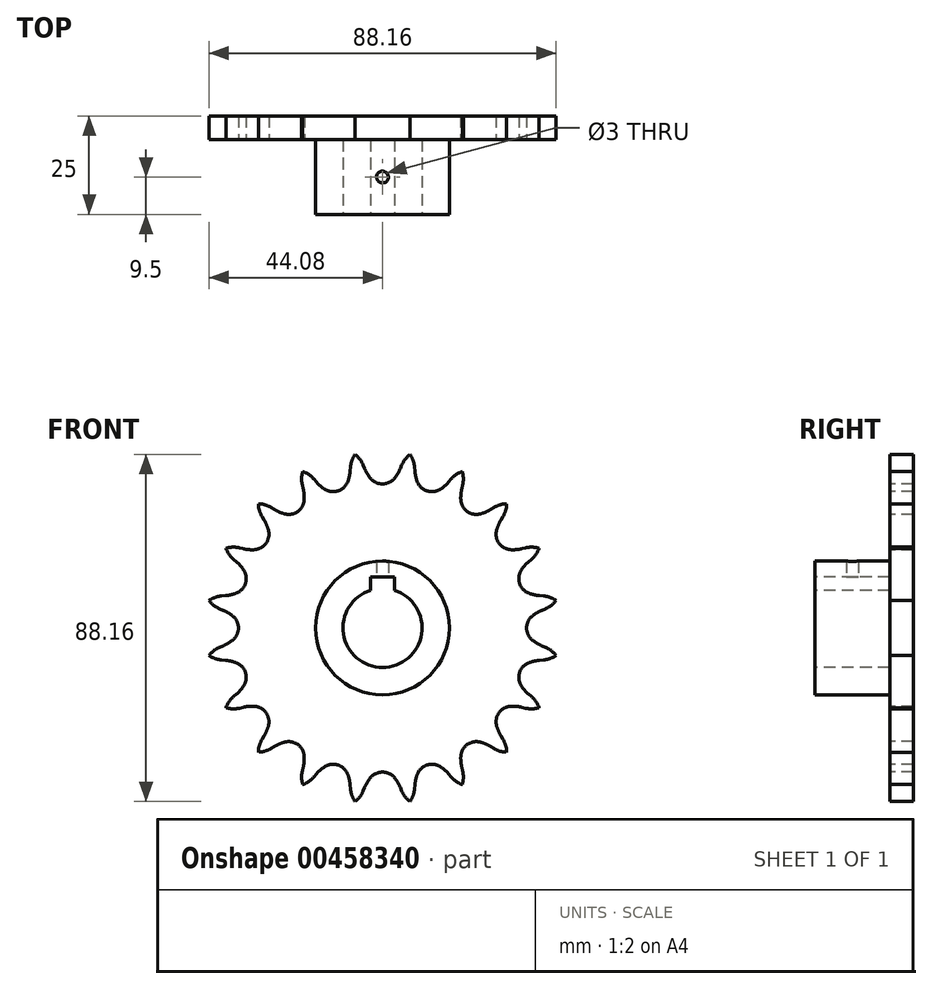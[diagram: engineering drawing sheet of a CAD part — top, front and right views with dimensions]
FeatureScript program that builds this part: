
annotation { "Feature Type Name" : "Feature", "Feature Type Description" : "" }
export const myFeature = defineFeature(function(context is Context, id is Id, definition is map)
    precondition{}
    {
        {
            var Q0;
            Q0=qCreatedBy(makeId("Front.planeOp"),FACE);
            var sketch = newSketch(context, id + "F0", { "sketchPlane" : qUnion([Q0])});
            skCircle(sketch, "E0", {"center": v(0, 0) * mm, "radius": 40.6 * mm, "construction": true});
            skLineSegment(sketch, "E1", {"start": v(0, 0) * mm, "end": v(0, 40.6) * mm, "construction": true});
            skLineSegment(sketch, "E2", {"start": v(0, 40.6) * mm, "end": v(73.85, 40.6) * mm, "construction": true});
            skArc(sketch, "E3", {"start": v(-3.14, 38.14) * mm, "mid": v(-1.75, 37.01) * mm, "end": v(0, 36.61) * mm});
            skLineSegment(sketch, "E4", {"start": v(0, 40.6) * mm, "end": v(5, 44.5) * mm, "construction": true});
            skLineSegment(sketch, "E5", {"start": v(5, 44.5) * mm, "end": v(-4.52, 40.5) * mm, "construction": true});
            skLineSegment(sketch, "E6", {"start": v(-4.52, 40.5) * mm, "end": v(-4.9, 41.4) * mm});
            skArc(sketch, "E7", {"start": v(-4.52, 40.5) * mm, "mid": v(-3.9, 39.27) * mm, "end": v(-3.14, 38.14) * mm});
            skArc(sketch, "E8", {"start": v(-17.18, 36.78) * mm, "mid": v(-9.17, 32.53) * mm, "end": v(-4.55, 40.34) * mm, "construction": true});
            skLineSegment(sketch, "E9", {"start": v(0, -0.5) * mm, "end": v(-9.94, 62.24) * mm, "construction": true});
            skArc(sketch, "E10.trimOffspring", {"start": v(-4.9, 41.4) * mm, "mid": v(-5.8, 42.92) * mm, "end": v(-7.07, 44.15) * mm});
            skArc(sketch, "E11.trimOffspring", {"start": v(0, 35.46) * mm, "mid": v(8.42, 34.76) * mm, "end": v(14.54, 40.6) * mm, "construction": true});
            skArc(sketch, "E12.trimOffspring", {"start": v(3.98, 40.4) * mm, "mid": v(3.98, 40.5) * mm, "end": v(3.98, 40.6) * mm, "construction": true});
            skArc(sketch, "E13.MirrorCS", {"start": v(4.9, 41.4) * mm, "mid": v(5.8, 42.92) * mm, "end": v(7.07, 44.15) * mm});
            skLineSegment(sketch, "E14.MirrorCS", {"start": v(4.52, 40.5) * mm, "end": v(4.9, 41.4) * mm});
            skArc(sketch, "E15.MirrorCS", {"start": v(4.52, 40.5) * mm, "mid": v(3.9, 39.27) * mm, "end": v(3.14, 38.14) * mm});
            skArc(sketch, "E16.MirrorCS", {"start": v(3.14, 38.14) * mm, "mid": v(1.75, 37.01) * mm, "end": v(0, 36.61) * mm});
            skArc(sketch, "E17.1.0", {"start": v(-8.14, 40.88) * mm, "mid": v(-7.75, 42.6) * mm, "end": v(-6.92, 44.17) * mm});
            skLineSegment(sketch, "E17.1.1", {"start": v(-8.22, 39.9) * mm, "end": v(-8.14, 40.88) * mm});
            skArc(sketch, "E17.1.2", {"start": v(-8.22, 39.9) * mm, "mid": v(-8.42, 38.56) * mm, "end": v(-8.8, 37.24) * mm});
            skArc(sketch, "E17.1.3", {"start": v(-8.8, 37.24) * mm, "mid": v(-9.78, 35.74) * mm, "end": v(-11.31, 34.82) * mm});
            skArc(sketch, "E17.1.4", {"start": v(-14.77, 35.3) * mm, "mid": v(-13.1, 34.66) * mm, "end": v(-11.31, 34.82) * mm});
            skArc(sketch, "E17.1.5", {"start": v(-16.81, 37.12) * mm, "mid": v(-15.85, 36.14) * mm, "end": v(-14.77, 35.3) * mm});
            skLineSegment(sketch, "E17.1.6", {"start": v(-16.81, 37.12) * mm, "end": v(-17.45, 37.85) * mm});
            skArc(sketch, "E17.1.7", {"start": v(-17.45, 37.85) * mm, "mid": v(-18.77, 39.03) * mm, "end": v(-20.37, 39.8) * mm});
            skArc(sketch, "E17.2.0", {"start": v(-20.37, 36.36) * mm, "mid": v(-20.54, 38.13) * mm, "end": v(-20.23, 39.87) * mm});
            skLineSegment(sketch, "E17.2.1", {"start": v(-20.15, 35.42) * mm, "end": v(-20.37, 36.36) * mm});
            skArc(sketch, "E17.2.2", {"start": v(-20.15, 35.42) * mm, "mid": v(-19.92, 34.07) * mm, "end": v(-19.88, 32.7) * mm});
            skArc(sketch, "E17.2.3", {"start": v(-19.88, 32.7) * mm, "mid": v(-20.34, 30.97) * mm, "end": v(-21.52, 29.62) * mm});
            skArc(sketch, "E17.2.4", {"start": v(-24.96, 29.01) * mm, "mid": v(-23.17, 28.92) * mm, "end": v(-21.52, 29.62) * mm});
            skArc(sketch, "E17.2.5", {"start": v(-27.46, 30.1) * mm, "mid": v(-26.24, 29.48) * mm, "end": v(-24.96, 29.01) * mm});
            skLineSegment(sketch, "E17.2.6", {"start": v(-27.46, 30.1) * mm, "end": v(-28.29, 30.6) * mm});
            skArc(sketch, "E17.2.7", {"start": v(-28.29, 30.6) * mm, "mid": v(-29.92, 31.31) * mm, "end": v(-31.67, 31.56) * mm});
            skArc(sketch, "E17.3.0", {"start": v(-30.6, 28.29) * mm, "mid": v(-31.31, 29.92) * mm, "end": v(-31.56, 31.67) * mm});
            skLineSegment(sketch, "E17.3.1", {"start": v(-30.1, 27.46) * mm, "end": v(-30.6, 28.29) * mm});
            skArc(sketch, "E17.3.2", {"start": v(-30.1, 27.46) * mm, "mid": v(-29.48, 26.24) * mm, "end": v(-29.01, 24.96) * mm});
            skArc(sketch, "E17.3.3", {"start": v(-29.01, 24.96) * mm, "mid": v(-28.92, 23.17) * mm, "end": v(-29.62, 21.52) * mm});
            skArc(sketch, "E17.3.4", {"start": v(-32.7, 19.88) * mm, "mid": v(-30.97, 20.34) * mm, "end": v(-29.62, 21.52) * mm});
            skArc(sketch, "E17.3.5", {"start": v(-35.42, 20.15) * mm, "mid": v(-34.07, 19.92) * mm, "end": v(-32.7, 19.88) * mm});
            skLineSegment(sketch, "E17.3.6", {"start": v(-35.42, 20.15) * mm, "end": v(-36.36, 20.37) * mm});
            skArc(sketch, "E17.3.7", {"start": v(-36.36, 20.37) * mm, "mid": v(-38.13, 20.54) * mm, "end": v(-39.87, 20.23) * mm});
            skArc(sketch, "E17.4.0", {"start": v(-37.85, 17.45) * mm, "mid": v(-39.03, 18.77) * mm, "end": v(-39.8, 20.37) * mm});
            skLineSegment(sketch, "E17.4.1", {"start": v(-37.12, 16.81) * mm, "end": v(-37.85, 17.45) * mm});
            skArc(sketch, "E17.4.2", {"start": v(-37.12, 16.81) * mm, "mid": v(-36.14, 15.85) * mm, "end": v(-35.3, 14.77) * mm});
            skArc(sketch, "E17.4.3", {"start": v(-35.3, 14.77) * mm, "mid": v(-34.66, 13.1) * mm, "end": v(-34.82, 11.31) * mm});
            skArc(sketch, "E17.4.4", {"start": v(-37.24, 8.8) * mm, "mid": v(-35.74, 9.78) * mm, "end": v(-34.82, 11.31) * mm});
            skArc(sketch, "E17.4.5", {"start": v(-39.9, 8.22) * mm, "mid": v(-38.56, 8.42) * mm, "end": v(-37.24, 8.8) * mm});
            skLineSegment(sketch, "E17.4.6", {"start": v(-39.9, 8.22) * mm, "end": v(-40.88, 8.14) * mm});
            skArc(sketch, "E17.4.7", {"start": v(-40.88, 8.14) * mm, "mid": v(-42.6, 7.75) * mm, "end": v(-44.17, 6.92) * mm});
            skArc(sketch, "E17.5.0", {"start": v(-41.4, 4.9) * mm, "mid": v(-42.92, 5.8) * mm, "end": v(-44.15, 7.07) * mm});
            skLineSegment(sketch, "E17.5.1", {"start": v(-40.5, 4.52) * mm, "end": v(-41.4, 4.9) * mm});
            skArc(sketch, "E17.5.2", {"start": v(-40.5, 4.52) * mm, "mid": v(-39.27, 3.9) * mm, "end": v(-38.14, 3.14) * mm});
            skArc(sketch, "E17.5.3", {"start": v(-38.14, 3.14) * mm, "mid": v(-37.01, 1.75) * mm, "end": v(-36.61, 0) * mm});
            skArc(sketch, "E17.5.4", {"start": v(-38.14, -3.14) * mm, "mid": v(-37.01, -1.75) * mm, "end": v(-36.61, 0) * mm});
            skArc(sketch, "E17.5.5", {"start": v(-40.5, -4.52) * mm, "mid": v(-39.27, -3.9) * mm, "end": v(-38.14, -3.14) * mm});
            skLineSegment(sketch, "E17.5.6", {"start": v(-40.5, -4.52) * mm, "end": v(-41.4, -4.9) * mm});
            skArc(sketch, "E17.5.7", {"start": v(-41.4, -4.9) * mm, "mid": v(-42.92, -5.8) * mm, "end": v(-44.15, -7.07) * mm});
            skArc(sketch, "E17.6.0", {"start": v(-40.88, -8.14) * mm, "mid": v(-42.6, -7.75) * mm, "end": v(-44.17, -6.92) * mm});
            skLineSegment(sketch, "E17.6.1", {"start": v(-39.9, -8.22) * mm, "end": v(-40.88, -8.14) * mm});
            skArc(sketch, "E17.6.2", {"start": v(-39.9, -8.22) * mm, "mid": v(-38.56, -8.42) * mm, "end": v(-37.24, -8.8) * mm});
            skArc(sketch, "E17.6.3", {"start": v(-37.24, -8.8) * mm, "mid": v(-35.74, -9.78) * mm, "end": v(-34.82, -11.31) * mm});
            skArc(sketch, "E17.6.4", {"start": v(-35.3, -14.77) * mm, "mid": v(-34.66, -13.1) * mm, "end": v(-34.82, -11.31) * mm});
            skArc(sketch, "E17.6.5", {"start": v(-37.12, -16.81) * mm, "mid": v(-36.14, -15.85) * mm, "end": v(-35.3, -14.77) * mm});
            skLineSegment(sketch, "E17.6.6", {"start": v(-37.12, -16.81) * mm, "end": v(-37.85, -17.45) * mm});
            skArc(sketch, "E17.6.7", {"start": v(-37.85, -17.45) * mm, "mid": v(-39.03, -18.77) * mm, "end": v(-39.8, -20.37) * mm});
            skArc(sketch, "E17.7.0", {"start": v(-36.36, -20.37) * mm, "mid": v(-38.13, -20.54) * mm, "end": v(-39.87, -20.23) * mm});
            skLineSegment(sketch, "E17.7.1", {"start": v(-35.42, -20.15) * mm, "end": v(-36.36, -20.37) * mm});
            skArc(sketch, "E17.7.2", {"start": v(-35.42, -20.15) * mm, "mid": v(-34.07, -19.92) * mm, "end": v(-32.7, -19.88) * mm});
            skArc(sketch, "E17.7.3", {"start": v(-32.7, -19.88) * mm, "mid": v(-30.97, -20.34) * mm, "end": v(-29.62, -21.52) * mm});
            skArc(sketch, "E17.7.4", {"start": v(-29.01, -24.96) * mm, "mid": v(-28.92, -23.17) * mm, "end": v(-29.62, -21.52) * mm});
            skArc(sketch, "E17.7.5", {"start": v(-30.1, -27.46) * mm, "mid": v(-29.48, -26.24) * mm, "end": v(-29.01, -24.96) * mm});
            skLineSegment(sketch, "E17.7.6", {"start": v(-30.1, -27.46) * mm, "end": v(-30.6, -28.29) * mm});
            skArc(sketch, "E17.7.7", {"start": v(-30.6, -28.29) * mm, "mid": v(-31.31, -29.92) * mm, "end": v(-31.56, -31.67) * mm});
            skArc(sketch, "E17.8.0", {"start": v(-28.29, -30.6) * mm, "mid": v(-29.92, -31.31) * mm, "end": v(-31.67, -31.56) * mm});
            skLineSegment(sketch, "E17.8.1", {"start": v(-27.46, -30.1) * mm, "end": v(-28.29, -30.6) * mm});
            skArc(sketch, "E17.8.2", {"start": v(-27.46, -30.1) * mm, "mid": v(-26.24, -29.48) * mm, "end": v(-24.96, -29.01) * mm});
            skArc(sketch, "E17.8.3", {"start": v(-24.96, -29.01) * mm, "mid": v(-23.17, -28.92) * mm, "end": v(-21.52, -29.62) * mm});
            skArc(sketch, "E17.8.4", {"start": v(-19.88, -32.7) * mm, "mid": v(-20.34, -30.97) * mm, "end": v(-21.52, -29.62) * mm});
            skArc(sketch, "E17.8.5", {"start": v(-20.15, -35.42) * mm, "mid": v(-19.92, -34.07) * mm, "end": v(-19.88, -32.7) * mm});
            skLineSegment(sketch, "E17.8.6", {"start": v(-20.15, -35.42) * mm, "end": v(-20.37, -36.36) * mm});
            skArc(sketch, "E17.8.7", {"start": v(-20.37, -36.36) * mm, "mid": v(-20.54, -38.13) * mm, "end": v(-20.23, -39.87) * mm});
            skArc(sketch, "E17.9.0", {"start": v(-17.45, -37.85) * mm, "mid": v(-18.77, -39.03) * mm, "end": v(-20.37, -39.8) * mm});
            skLineSegment(sketch, "E17.9.1", {"start": v(-16.81, -37.12) * mm, "end": v(-17.45, -37.85) * mm});
            skArc(sketch, "E17.9.2", {"start": v(-16.81, -37.12) * mm, "mid": v(-15.85, -36.14) * mm, "end": v(-14.77, -35.3) * mm});
            skArc(sketch, "E17.9.3", {"start": v(-14.77, -35.3) * mm, "mid": v(-13.1, -34.66) * mm, "end": v(-11.31, -34.82) * mm});
            skArc(sketch, "E17.9.4", {"start": v(-8.8, -37.24) * mm, "mid": v(-9.78, -35.74) * mm, "end": v(-11.31, -34.82) * mm});
            skArc(sketch, "E17.9.5", {"start": v(-8.22, -39.9) * mm, "mid": v(-8.42, -38.56) * mm, "end": v(-8.8, -37.24) * mm});
            skLineSegment(sketch, "E17.9.6", {"start": v(-8.22, -39.9) * mm, "end": v(-8.14, -40.88) * mm});
            skArc(sketch, "E17.9.7", {"start": v(-8.14, -40.88) * mm, "mid": v(-7.75, -42.6) * mm, "end": v(-6.92, -44.17) * mm});
            skArc(sketch, "E17.10.0", {"start": v(-4.9, -41.4) * mm, "mid": v(-5.8, -42.92) * mm, "end": v(-7.07, -44.15) * mm});
            skLineSegment(sketch, "E17.10.1", {"start": v(-4.52, -40.5) * mm, "end": v(-4.9, -41.4) * mm});
            skArc(sketch, "E17.10.2", {"start": v(-4.52, -40.5) * mm, "mid": v(-3.9, -39.27) * mm, "end": v(-3.14, -38.14) * mm});
            skArc(sketch, "E17.10.3", {"start": v(-3.14, -38.14) * mm, "mid": v(-1.75, -37.01) * mm, "end": v(0, -36.61) * mm});
            skArc(sketch, "E17.10.4", {"start": v(3.14, -38.14) * mm, "mid": v(1.75, -37.01) * mm, "end": v(0, -36.61) * mm});
            skArc(sketch, "E17.10.5", {"start": v(4.52, -40.5) * mm, "mid": v(3.9, -39.27) * mm, "end": v(3.14, -38.14) * mm});
            skLineSegment(sketch, "E17.10.6", {"start": v(4.52, -40.5) * mm, "end": v(4.9, -41.4) * mm});
            skArc(sketch, "E17.10.7", {"start": v(4.9, -41.4) * mm, "mid": v(5.8, -42.92) * mm, "end": v(7.07, -44.15) * mm});
            skArc(sketch, "E17.11.0", {"start": v(8.14, -40.88) * mm, "mid": v(7.75, -42.6) * mm, "end": v(6.92, -44.17) * mm});
            skLineSegment(sketch, "E17.11.1", {"start": v(8.22, -39.9) * mm, "end": v(8.14, -40.88) * mm});
            skArc(sketch, "E17.11.2", {"start": v(8.22, -39.9) * mm, "mid": v(8.42, -38.56) * mm, "end": v(8.8, -37.24) * mm});
            skArc(sketch, "E17.11.3", {"start": v(8.8, -37.24) * mm, "mid": v(9.78, -35.74) * mm, "end": v(11.31, -34.82) * mm});
            skArc(sketch, "E17.11.4", {"start": v(14.77, -35.3) * mm, "mid": v(13.1, -34.66) * mm, "end": v(11.31, -34.82) * mm});
            skArc(sketch, "E17.11.5", {"start": v(16.81, -37.12) * mm, "mid": v(15.85, -36.14) * mm, "end": v(14.77, -35.3) * mm});
            skLineSegment(sketch, "E17.11.6", {"start": v(16.81, -37.12) * mm, "end": v(17.45, -37.85) * mm});
            skArc(sketch, "E17.11.7", {"start": v(17.45, -37.85) * mm, "mid": v(18.77, -39.03) * mm, "end": v(20.37, -39.8) * mm});
            skArc(sketch, "E17.12.0", {"start": v(20.37, -36.36) * mm, "mid": v(20.54, -38.13) * mm, "end": v(20.23, -39.87) * mm});
            skLineSegment(sketch, "E17.12.1", {"start": v(20.15, -35.42) * mm, "end": v(20.37, -36.36) * mm});
            skArc(sketch, "E17.12.2", {"start": v(20.15, -35.42) * mm, "mid": v(19.92, -34.07) * mm, "end": v(19.88, -32.7) * mm});
            skArc(sketch, "E17.12.3", {"start": v(19.88, -32.7) * mm, "mid": v(20.34, -30.97) * mm, "end": v(21.52, -29.62) * mm});
            skArc(sketch, "E17.12.4", {"start": v(24.96, -29.01) * mm, "mid": v(23.17, -28.92) * mm, "end": v(21.52, -29.62) * mm});
            skArc(sketch, "E17.12.5", {"start": v(27.46, -30.1) * mm, "mid": v(26.24, -29.48) * mm, "end": v(24.96, -29.01) * mm});
            skLineSegment(sketch, "E17.12.6", {"start": v(27.46, -30.1) * mm, "end": v(28.29, -30.6) * mm});
            skArc(sketch, "E17.12.7", {"start": v(28.29, -30.6) * mm, "mid": v(29.92, -31.31) * mm, "end": v(31.67, -31.56) * mm});
            skArc(sketch, "E17.13.0", {"start": v(30.6, -28.29) * mm, "mid": v(31.31, -29.92) * mm, "end": v(31.56, -31.67) * mm});
            skLineSegment(sketch, "E17.13.1", {"start": v(30.1, -27.46) * mm, "end": v(30.6, -28.29) * mm});
            skArc(sketch, "E17.13.2", {"start": v(30.1, -27.46) * mm, "mid": v(29.48, -26.24) * mm, "end": v(29.01, -24.96) * mm});
            skArc(sketch, "E17.13.3", {"start": v(29.01, -24.96) * mm, "mid": v(28.92, -23.17) * mm, "end": v(29.62, -21.52) * mm});
            skArc(sketch, "E17.13.4", {"start": v(32.7, -19.88) * mm, "mid": v(30.97, -20.34) * mm, "end": v(29.62, -21.52) * mm});
            skArc(sketch, "E17.13.5", {"start": v(35.42, -20.15) * mm, "mid": v(34.07, -19.92) * mm, "end": v(32.7, -19.88) * mm});
            skLineSegment(sketch, "E17.13.6", {"start": v(35.42, -20.15) * mm, "end": v(36.36, -20.37) * mm});
            skArc(sketch, "E17.13.7", {"start": v(36.36, -20.37) * mm, "mid": v(38.13, -20.54) * mm, "end": v(39.87, -20.23) * mm});
            skArc(sketch, "E17.14.0", {"start": v(37.85, -17.45) * mm, "mid": v(39.03, -18.77) * mm, "end": v(39.8, -20.37) * mm});
            skLineSegment(sketch, "E17.14.1", {"start": v(37.12, -16.81) * mm, "end": v(37.85, -17.45) * mm});
            skArc(sketch, "E17.14.2", {"start": v(37.12, -16.81) * mm, "mid": v(36.14, -15.85) * mm, "end": v(35.3, -14.77) * mm});
            skArc(sketch, "E17.14.3", {"start": v(35.3, -14.77) * mm, "mid": v(34.66, -13.1) * mm, "end": v(34.82, -11.31) * mm});
            skArc(sketch, "E17.14.4", {"start": v(37.24, -8.8) * mm, "mid": v(35.74, -9.78) * mm, "end": v(34.82, -11.31) * mm});
            skArc(sketch, "E17.14.5", {"start": v(39.9, -8.22) * mm, "mid": v(38.56, -8.42) * mm, "end": v(37.24, -8.8) * mm});
            skLineSegment(sketch, "E17.14.6", {"start": v(39.9, -8.22) * mm, "end": v(40.88, -8.14) * mm});
            skArc(sketch, "E17.14.7", {"start": v(40.88, -8.14) * mm, "mid": v(42.6, -7.75) * mm, "end": v(44.17, -6.92) * mm});
            skArc(sketch, "E17.15.0", {"start": v(41.4, -4.9) * mm, "mid": v(42.92, -5.8) * mm, "end": v(44.15, -7.07) * mm});
            skLineSegment(sketch, "E17.15.1", {"start": v(40.5, -4.52) * mm, "end": v(41.4, -4.9) * mm});
            skArc(sketch, "E17.15.2", {"start": v(40.5, -4.52) * mm, "mid": v(39.27, -3.9) * mm, "end": v(38.14, -3.14) * mm});
            skArc(sketch, "E17.15.3", {"start": v(38.14, -3.14) * mm, "mid": v(37.01, -1.75) * mm, "end": v(36.61, 0) * mm});
            skArc(sketch, "E17.15.4", {"start": v(38.14, 3.14) * mm, "mid": v(37.01, 1.75) * mm, "end": v(36.61, 0) * mm});
            skArc(sketch, "E17.15.5", {"start": v(40.5, 4.52) * mm, "mid": v(39.27, 3.9) * mm, "end": v(38.14, 3.14) * mm});
            skLineSegment(sketch, "E17.15.6", {"start": v(40.5, 4.52) * mm, "end": v(41.4, 4.9) * mm});
            skArc(sketch, "E17.15.7", {"start": v(41.4, 4.9) * mm, "mid": v(42.92, 5.8) * mm, "end": v(44.15, 7.07) * mm});
            skArc(sketch, "E17.16.0", {"start": v(40.88, 8.14) * mm, "mid": v(42.6, 7.75) * mm, "end": v(44.17, 6.92) * mm});
            skLineSegment(sketch, "E17.16.1", {"start": v(39.9, 8.22) * mm, "end": v(40.88, 8.14) * mm});
            skArc(sketch, "E17.16.2", {"start": v(39.9, 8.22) * mm, "mid": v(38.56, 8.42) * mm, "end": v(37.24, 8.8) * mm});
            skArc(sketch, "E17.16.3", {"start": v(37.24, 8.8) * mm, "mid": v(35.74, 9.78) * mm, "end": v(34.82, 11.31) * mm});
            skArc(sketch, "E17.16.4", {"start": v(35.3, 14.77) * mm, "mid": v(34.66, 13.1) * mm, "end": v(34.82, 11.31) * mm});
            skArc(sketch, "E17.16.5", {"start": v(37.12, 16.81) * mm, "mid": v(36.14, 15.85) * mm, "end": v(35.3, 14.77) * mm});
            skLineSegment(sketch, "E17.16.6", {"start": v(37.12, 16.81) * mm, "end": v(37.85, 17.45) * mm});
            skArc(sketch, "E17.16.7", {"start": v(37.85, 17.45) * mm, "mid": v(39.03, 18.77) * mm, "end": v(39.8, 20.37) * mm});
            skArc(sketch, "E17.17.0", {"start": v(36.36, 20.37) * mm, "mid": v(38.13, 20.54) * mm, "end": v(39.87, 20.23) * mm});
            skLineSegment(sketch, "E17.17.1", {"start": v(35.42, 20.15) * mm, "end": v(36.36, 20.37) * mm});
            skArc(sketch, "E17.17.2", {"start": v(35.42, 20.15) * mm, "mid": v(34.07, 19.92) * mm, "end": v(32.7, 19.88) * mm});
            skArc(sketch, "E17.17.3", {"start": v(32.7, 19.88) * mm, "mid": v(30.97, 20.34) * mm, "end": v(29.62, 21.52) * mm});
            skArc(sketch, "E17.17.4", {"start": v(29.01, 24.96) * mm, "mid": v(28.92, 23.17) * mm, "end": v(29.62, 21.52) * mm});
            skArc(sketch, "E17.17.5", {"start": v(30.1, 27.46) * mm, "mid": v(29.48, 26.24) * mm, "end": v(29.01, 24.96) * mm});
            skLineSegment(sketch, "E17.17.6", {"start": v(30.1, 27.46) * mm, "end": v(30.6, 28.29) * mm});
            skArc(sketch, "E17.17.7", {"start": v(30.6, 28.29) * mm, "mid": v(31.31, 29.92) * mm, "end": v(31.56, 31.67) * mm});
            skArc(sketch, "E17.18.0", {"start": v(28.29, 30.6) * mm, "mid": v(29.92, 31.31) * mm, "end": v(31.67, 31.56) * mm});
            skLineSegment(sketch, "E17.18.1", {"start": v(27.46, 30.1) * mm, "end": v(28.29, 30.6) * mm});
            skArc(sketch, "E17.18.2", {"start": v(27.46, 30.1) * mm, "mid": v(26.24, 29.48) * mm, "end": v(24.96, 29.01) * mm});
            skArc(sketch, "E17.18.3", {"start": v(24.96, 29.01) * mm, "mid": v(23.17, 28.92) * mm, "end": v(21.52, 29.62) * mm});
            skArc(sketch, "E17.18.4", {"start": v(19.88, 32.7) * mm, "mid": v(20.34, 30.97) * mm, "end": v(21.52, 29.62) * mm});
            skArc(sketch, "E17.18.5", {"start": v(20.15, 35.42) * mm, "mid": v(19.92, 34.07) * mm, "end": v(19.88, 32.7) * mm});
            skLineSegment(sketch, "E17.18.6", {"start": v(20.15, 35.42) * mm, "end": v(20.37, 36.36) * mm});
            skArc(sketch, "E17.18.7", {"start": v(20.37, 36.36) * mm, "mid": v(20.54, 38.13) * mm, "end": v(20.23, 39.87) * mm});
            skArc(sketch, "E17.19.0", {"start": v(17.45, 37.85) * mm, "mid": v(18.77, 39.03) * mm, "end": v(20.37, 39.8) * mm});
            skLineSegment(sketch, "E17.19.1", {"start": v(16.81, 37.12) * mm, "end": v(17.45, 37.85) * mm});
            skArc(sketch, "E17.19.2", {"start": v(16.81, 37.12) * mm, "mid": v(15.85, 36.14) * mm, "end": v(14.77, 35.3) * mm});
            skArc(sketch, "E17.19.3", {"start": v(14.77, 35.3) * mm, "mid": v(13.1, 34.66) * mm, "end": v(11.31, 34.82) * mm});
            skArc(sketch, "E17.19.4", {"start": v(8.8, 37.24) * mm, "mid": v(9.78, 35.74) * mm, "end": v(11.31, 34.82) * mm});
            skArc(sketch, "E17.19.5", {"start": v(8.22, 39.9) * mm, "mid": v(8.42, 38.56) * mm, "end": v(8.8, 37.24) * mm});
            skLineSegment(sketch, "E17.19.6", {"start": v(8.22, 39.9) * mm, "end": v(8.14, 40.88) * mm});
            skArc(sketch, "E17.19.7", {"start": v(8.14, 40.88) * mm, "mid": v(7.75, 42.6) * mm, "end": v(6.92, 44.17) * mm});
            skSolve(sketch);
        }
        {
            var Q0;
            Q0=makeQuery(id+"F0.imprint","IMPRINT",FACE,{"disambiguationData":[TD([[makeQuery(id+"F0.imprint","IMPRINT",EDGE,{"derivedFrom":sQuery(id+"F0.wireOp",EDGE,"E3")}),-1.0]])]});
            extrude(context, id + "F1", {"entities" : qUnion([Q0]), "depth" : -6 * mm, "offsetDistance" : 25 * mm});
        }
        {
            var Q0;
            Q0=makeQuery(id+"F1.opExtrude","CAP_FACE",FACE,{"disambiguationData":[OSD([sQuery(id+"F0.wireOp",EDGE,"E3"),sQuery(id+"F0.wireOp",EDGE,"E6"),sQuery(id+"F0.wireOp",EDGE,"E7"),sQuery(id+"F0.wireOp",EDGE,"E10.trimOffspring"),sQuery(id+"F0.wireOp",EDGE,"E13.MirrorCS"),sQuery(id+"F0.wireOp",EDGE,"E14.MirrorCS"),sQuery(id+"F0.wireOp",EDGE,"E15.MirrorCS"),sQuery(id+"F0.wireOp",EDGE,"E16.MirrorCS"),sQuery(id+"F0.wireOp",EDGE,"E17.1.0"),sQuery(id+"F0.wireOp",EDGE,"E17.1.1"),sQuery(id+"F0.wireOp",EDGE,"E17.1.2"),sQuery(id+"F0.wireOp",EDGE,"E17.1.3"),sQuery(id+"F0.wireOp",EDGE,"E17.1.4"),sQuery(id+"F0.wireOp",EDGE,"E17.1.5"),sQuery(id+"F0.wireOp",EDGE,"E17.1.6"),sQuery(id+"F0.wireOp",EDGE,"E17.1.7"),sQuery(id+"F0.wireOp",EDGE,"E17.2.0"),sQuery(id+"F0.wireOp",EDGE,"E17.2.1"),sQuery(id+"F0.wireOp",EDGE,"E17.2.2"),sQuery(id+"F0.wireOp",EDGE,"E17.2.3"),sQuery(id+"F0.wireOp",EDGE,"E17.2.4"),sQuery(id+"F0.wireOp",EDGE,"E17.2.5"),sQuery(id+"F0.wireOp",EDGE,"E17.2.6"),sQuery(id+"F0.wireOp",EDGE,"E17.2.7"),sQuery(id+"F0.wireOp",EDGE,"E17.3.0"),sQuery(id+"F0.wireOp",EDGE,"E17.3.1"),sQuery(id+"F0.wireOp",EDGE,"E17.3.2"),sQuery(id+"F0.wireOp",EDGE,"E17.3.3"),sQuery(id+"F0.wireOp",EDGE,"E17.3.4"),sQuery(id+"F0.wireOp",EDGE,"E17.3.5"),sQuery(id+"F0.wireOp",EDGE,"E17.3.6"),sQuery(id+"F0.wireOp",EDGE,"E17.3.7"),sQuery(id+"F0.wireOp",EDGE,"E17.4.0"),sQuery(id+"F0.wireOp",EDGE,"E17.4.1"),sQuery(id+"F0.wireOp",EDGE,"E17.4.2"),sQuery(id+"F0.wireOp",EDGE,"E17.4.3"),sQuery(id+"F0.wireOp",EDGE,"E17.4.4"),sQuery(id+"F0.wireOp",EDGE,"E17.4.5"),sQuery(id+"F0.wireOp",EDGE,"E17.4.6"),sQuery(id+"F0.wireOp",EDGE,"E17.4.7"),sQuery(id+"F0.wireOp",EDGE,"E17.5.0"),sQuery(id+"F0.wireOp",EDGE,"E17.5.1"),sQuery(id+"F0.wireOp",EDGE,"E17.5.2"),sQuery(id+"F0.wireOp",EDGE,"E17.5.3"),sQuery(id+"F0.wireOp",EDGE,"E17.5.4"),sQuery(id+"F0.wireOp",EDGE,"E17.5.5"),sQuery(id+"F0.wireOp",EDGE,"E17.5.6"),sQuery(id+"F0.wireOp",EDGE,"E17.5.7"),sQuery(id+"F0.wireOp",EDGE,"E17.6.0"),sQuery(id+"F0.wireOp",EDGE,"E17.6.1"),sQuery(id+"F0.wireOp",EDGE,"E17.6.2"),sQuery(id+"F0.wireOp",EDGE,"E17.6.3"),sQuery(id+"F0.wireOp",EDGE,"E17.6.4"),sQuery(id+"F0.wireOp",EDGE,"E17.6.5"),sQuery(id+"F0.wireOp",EDGE,"E17.6.6"),sQuery(id+"F0.wireOp",EDGE,"E17.6.7"),sQuery(id+"F0.wireOp",EDGE,"E17.7.0"),sQuery(id+"F0.wireOp",EDGE,"E17.7.1"),sQuery(id+"F0.wireOp",EDGE,"E17.7.2"),sQuery(id+"F0.wireOp",EDGE,"E17.7.3"),sQuery(id+"F0.wireOp",EDGE,"E17.7.4"),sQuery(id+"F0.wireOp",EDGE,"E17.7.5"),sQuery(id+"F0.wireOp",EDGE,"E17.7.6"),sQuery(id+"F0.wireOp",EDGE,"E17.7.7"),sQuery(id+"F0.wireOp",EDGE,"E17.8.0"),sQuery(id+"F0.wireOp",EDGE,"E17.8.1"),sQuery(id+"F0.wireOp",EDGE,"E17.8.2"),sQuery(id+"F0.wireOp",EDGE,"E17.8.3"),sQuery(id+"F0.wireOp",EDGE,"E17.8.4"),sQuery(id+"F0.wireOp",EDGE,"E17.8.5"),sQuery(id+"F0.wireOp",EDGE,"E17.8.6"),sQuery(id+"F0.wireOp",EDGE,"E17.8.7"),sQuery(id+"F0.wireOp",EDGE,"E17.9.0"),sQuery(id+"F0.wireOp",EDGE,"E17.9.1"),sQuery(id+"F0.wireOp",EDGE,"E17.9.2"),sQuery(id+"F0.wireOp",EDGE,"E17.9.3"),sQuery(id+"F0.wireOp",EDGE,"E17.9.4"),sQuery(id+"F0.wireOp",EDGE,"E17.9.5"),sQuery(id+"F0.wireOp",EDGE,"E17.9.6"),sQuery(id+"F0.wireOp",EDGE,"E17.9.7"),sQuery(id+"F0.wireOp",EDGE,"E17.10.0"),sQuery(id+"F0.wireOp",EDGE,"E17.10.1"),sQuery(id+"F0.wireOp",EDGE,"E17.10.2"),sQuery(id+"F0.wireOp",EDGE,"E17.10.3"),sQuery(id+"F0.wireOp",EDGE,"E17.10.4"),sQuery(id+"F0.wireOp",EDGE,"E17.10.5"),sQuery(id+"F0.wireOp",EDGE,"E17.10.6"),sQuery(id+"F0.wireOp",EDGE,"E17.10.7"),sQuery(id+"F0.wireOp",EDGE,"E17.11.0"),sQuery(id+"F0.wireOp",EDGE,"E17.11.1"),sQuery(id+"F0.wireOp",EDGE,"E17.11.2"),sQuery(id+"F0.wireOp",EDGE,"E17.11.3"),sQuery(id+"F0.wireOp",EDGE,"E17.11.4"),sQuery(id+"F0.wireOp",EDGE,"E17.11.5"),sQuery(id+"F0.wireOp",EDGE,"E17.11.6"),sQuery(id+"F0.wireOp",EDGE,"E17.11.7"),sQuery(id+"F0.wireOp",EDGE,"E17.12.0"),sQuery(id+"F0.wireOp",EDGE,"E17.12.1"),sQuery(id+"F0.wireOp",EDGE,"E17.12.2"),sQuery(id+"F0.wireOp",EDGE,"E17.12.3"),sQuery(id+"F0.wireOp",EDGE,"E17.12.4"),sQuery(id+"F0.wireOp",EDGE,"E17.12.5"),sQuery(id+"F0.wireOp",EDGE,"E17.12.6"),sQuery(id+"F0.wireOp",EDGE,"E17.12.7"),sQuery(id+"F0.wireOp",EDGE,"E17.13.0"),sQuery(id+"F0.wireOp",EDGE,"E17.13.1"),sQuery(id+"F0.wireOp",EDGE,"E17.13.2"),sQuery(id+"F0.wireOp",EDGE,"E17.13.3"),sQuery(id+"F0.wireOp",EDGE,"E17.13.4"),sQuery(id+"F0.wireOp",EDGE,"E17.13.5"),sQuery(id+"F0.wireOp",EDGE,"E17.13.6"),sQuery(id+"F0.wireOp",EDGE,"E17.13.7"),sQuery(id+"F0.wireOp",EDGE,"E17.14.0"),sQuery(id+"F0.wireOp",EDGE,"E17.14.1"),sQuery(id+"F0.wireOp",EDGE,"E17.14.2"),sQuery(id+"F0.wireOp",EDGE,"E17.14.3"),sQuery(id+"F0.wireOp",EDGE,"E17.14.4"),sQuery(id+"F0.wireOp",EDGE,"E17.14.5"),sQuery(id+"F0.wireOp",EDGE,"E17.14.6"),sQuery(id+"F0.wireOp",EDGE,"E17.14.7"),sQuery(id+"F0.wireOp",EDGE,"E17.15.0"),sQuery(id+"F0.wireOp",EDGE,"E17.15.1"),sQuery(id+"F0.wireOp",EDGE,"E17.15.2"),sQuery(id+"F0.wireOp",EDGE,"E17.15.3"),sQuery(id+"F0.wireOp",EDGE,"E17.15.4"),sQuery(id+"F0.wireOp",EDGE,"E17.15.5"),sQuery(id+"F0.wireOp",EDGE,"E17.15.6"),sQuery(id+"F0.wireOp",EDGE,"E17.15.7"),sQuery(id+"F0.wireOp",EDGE,"E17.16.0"),sQuery(id+"F0.wireOp",EDGE,"E17.16.1"),sQuery(id+"F0.wireOp",EDGE,"E17.16.2"),sQuery(id+"F0.wireOp",EDGE,"E17.16.3"),sQuery(id+"F0.wireOp",EDGE,"E17.16.4"),sQuery(id+"F0.wireOp",EDGE,"E17.16.5"),sQuery(id+"F0.wireOp",EDGE,"E17.16.6"),sQuery(id+"F0.wireOp",EDGE,"E17.16.7"),sQuery(id+"F0.wireOp",EDGE,"E17.17.0"),sQuery(id+"F0.wireOp",EDGE,"E17.17.1"),sQuery(id+"F0.wireOp",EDGE,"E17.17.2"),sQuery(id+"F0.wireOp",EDGE,"E17.17.3"),sQuery(id+"F0.wireOp",EDGE,"E17.17.4"),sQuery(id+"F0.wireOp",EDGE,"E17.17.5"),sQuery(id+"F0.wireOp",EDGE,"E17.17.6"),sQuery(id+"F0.wireOp",EDGE,"E17.17.7"),sQuery(id+"F0.wireOp",EDGE,"E17.18.0"),sQuery(id+"F0.wireOp",EDGE,"E17.18.1"),sQuery(id+"F0.wireOp",EDGE,"E17.18.2"),sQuery(id+"F0.wireOp",EDGE,"E17.18.3"),sQuery(id+"F0.wireOp",EDGE,"E17.18.4"),sQuery(id+"F0.wireOp",EDGE,"E17.18.5"),sQuery(id+"F0.wireOp",EDGE,"E17.18.6"),sQuery(id+"F0.wireOp",EDGE,"E17.18.7"),sQuery(id+"F0.wireOp",EDGE,"E17.19.0"),sQuery(id+"F0.wireOp",EDGE,"E17.19.1"),sQuery(id+"F0.wireOp",EDGE,"E17.19.2"),sQuery(id+"F0.wireOp",EDGE,"E17.19.3"),sQuery(id+"F0.wireOp",EDGE,"E17.19.4"),sQuery(id+"F0.wireOp",EDGE,"E17.19.5"),sQuery(id+"F0.wireOp",EDGE,"E17.19.6"),sQuery(id+"F0.wireOp",EDGE,"E17.19.7")])],"isStart":true});
            var sketch = newSketch(context, id + "F2", { "sketchPlane" : qUnion([Q0])});
            skCircle(sketch, "E18", {"center": v(0, 0) * mm, "radius": 17 * mm});
            skSolve(sketch);
        }
        {
            var Q0;
            Q0=makeQuery(id+"F2.imprint","IMPRINT",FACE,{"disambiguationData":[TD([[makeQuery(id+"F2.imprint","IMPRINT",EDGE,{"derivedFrom":sQuery(id+"F2.wireOp",EDGE,"E18")}),1.0]])]});
            extrude(context, id + "F3", {"entities" : qUnion([Q0]), "operationType" : NewBodyOperationType.ADD, "depth" : 19 * mm, "offsetDistance" : 25 * mm});
        }
        {
            var Q0;
            Q0=makeQuery(id+"F3.opExtrude","CAP_FACE",FACE,{"disambiguationData":[OSD([sQuery(id+"F2.wireOp",EDGE,"E18")])],"isStart":false});
            var sketch = newSketch(context, id + "F4", { "sketchPlane" : qUnion([Q0])});
            skArc(sketch, "E19", {"start": v(-3, 9.6) * mm, "mid": v(0, -10.05) * mm, "end": v(3, 9.6) * mm});
            skLineSegment(sketch, "E20.top", {"start": v(-3, 13) * mm, "end": v(3, 13) * mm});
            skLineSegment(sketch, "E20.left", {"start": v(-3, 9.6) * mm, "end": v(-3, 13) * mm});
            skLineSegment(sketch, "E20.right", {"start": v(3, 9.6) * mm, "end": v(3, 13) * mm});
            skPoint(sketch, "E21.orphan", {"position": v(-3, 0) * mm});
            skSolve(sketch);
        }
        {
            var Q0;
            Q0=makeQuery(id+"F4.imprint","IMPRINT",FACE,{"disambiguationData":[TD([[makeQuery(id+"F4.imprint","IMPRINT",EDGE,{"derivedFrom":sQuery(id+"F4.wireOp",EDGE,"E19")}),1.0]])]});
            extrude(context, id + "F5", {"entities" : qUnion([Q0]), "operationType" : NewBodyOperationType.REMOVE, "oppositeDirection" : true, "depth" : 19 * mm, "offsetDistance" : 25 * mm});
        }
        {
            var Q0;
            Q0=qCreatedBy(makeId("Top.planeOp"),FACE);
            var sketch = newSketch(context, id + "F6", { "sketchPlane" : qUnion([Q0])});
            skCircle(sketch, "E22", {"center": v(0, -9.5) * mm, "radius": 1.5 * mm});
            skSolve(sketch);
        }
        {
            var Q0;
            Q0=makeQuery(id+"F6.imprint","IMPRINT",FACE,{"disambiguationData":[TD([[makeQuery(id+"F6.imprint","IMPRINT",EDGE,{"derivedFrom":sQuery(id+"F6.wireOp",EDGE,"E22")}),1.0]])]});
            extrude(context, id + "F7", {"entities" : qUnion([Q0]), "operationType" : NewBodyOperationType.REMOVE, "depth" : 25 * mm, "offsetDistance" : 25 * mm});
        }
    });
